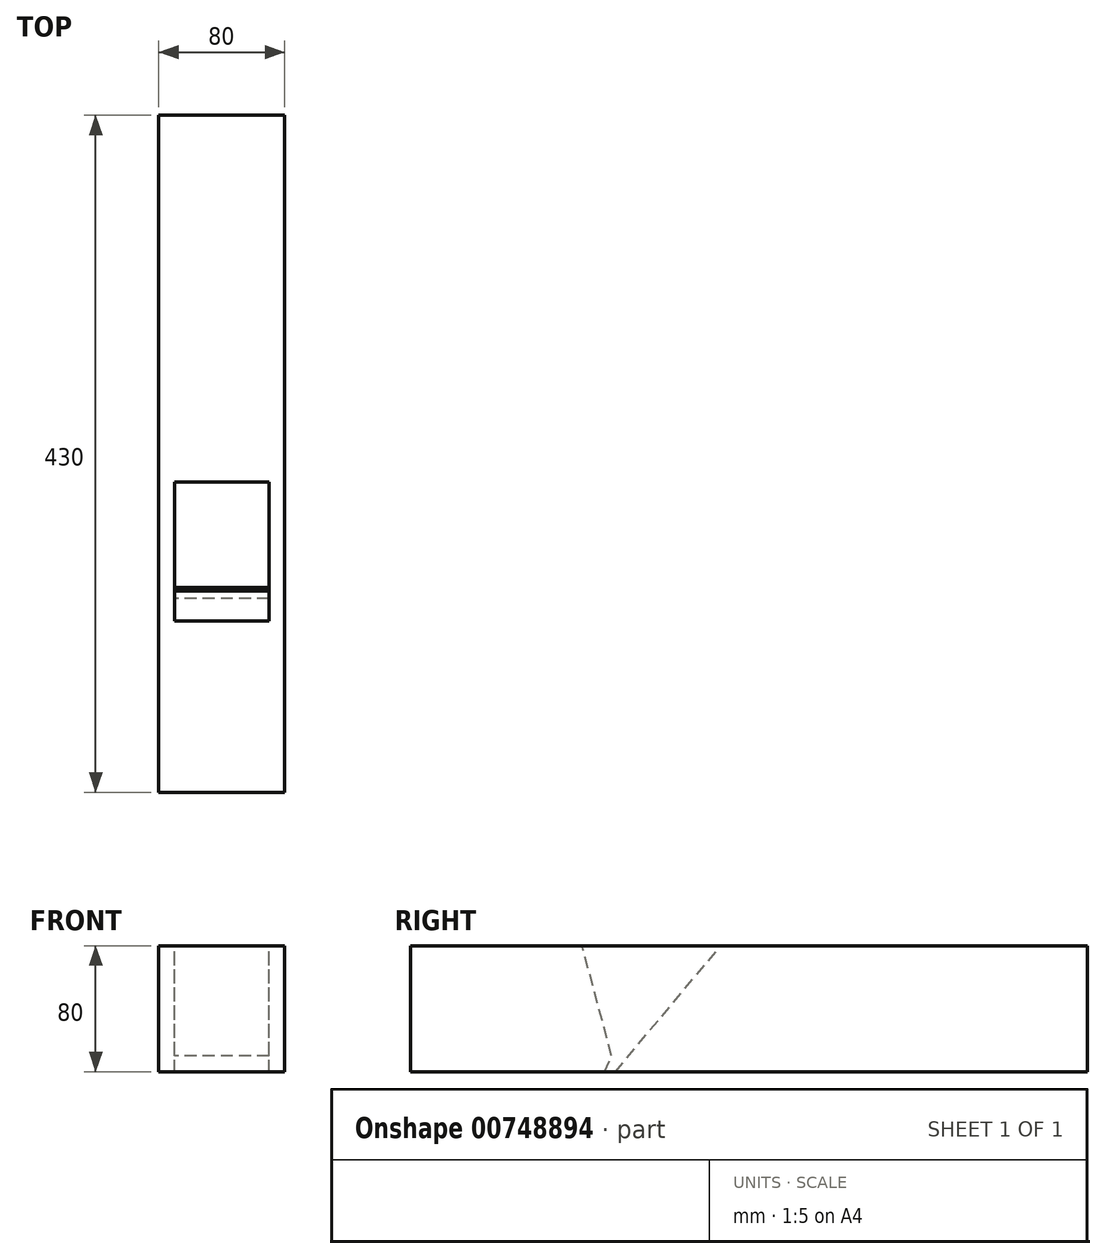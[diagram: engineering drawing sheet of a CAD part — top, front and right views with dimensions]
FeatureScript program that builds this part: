
annotation { "Feature Type Name" : "Feature", "Feature Type Description" : "" }
export const myFeature = defineFeature(function(context is Context, id is Id, definition is map)
    precondition{}
    {
        {
            var Q0;
            Q0=qCreatedBy(makeId("Right.planeOp"),FACE);
            var sketch = newSketch(context, id + "F0", { "sketchPlane" : qUnion([Q0])});
            skLineSegment(sketch, "E0.bottom", {"start": v(215, -40) * mm, "end": v(-215, -40) * mm});
            skLineSegment(sketch, "E0.top", {"start": v(215, 40) * mm, "end": v(-215, 40) * mm});
            skLineSegment(sketch, "E0.left", {"start": v(215, -40) * mm, "end": v(215, 40) * mm});
            skLineSegment(sketch, "E0.right", {"start": v(-215, -40) * mm, "end": v(-215, 40) * mm});
            skPoint(sketch, "E0.middle", {"position": v(0, 0) * mm});
            skSolve(sketch);
        }
        {
            var Q0;
            Q0=makeQuery(id+"F0.imprint","IMPRINT",FACE,{"disambiguationData":[TD([[makeQuery(id+"F0.imprint","IMPRINT",EDGE,{"derivedFrom":sQuery(id+"F0.wireOp",EDGE,"E0.bottom")}),-1.0]])]});
            extrude(context, id + "F1", {"entities" : qUnion([Q0]), "endBound" : BoundingType.SYMMETRIC, "depth" : 80 * mm, "offsetDistance" : 25 * mm});
        }
        {
            var Q0;
            Q0=qCreatedBy(makeId("Right.planeOp"),FACE);
            var sketch = newSketch(context, id + "F2", { "sketchPlane" : qUnion([Q0])});
            skLineSegment(sketch, "E1.bottom", {"start": v(-85, -40) * mm, "end": v(-92, -40) * mm});
            skLineSegment(sketch, "E1.left", {"start": v(215, -40) * mm, "end": v(215, 40) * mm});
            skPoint(sketch, "E1.middle", {"position": v(0, 0) * mm});
            skLineSegment(sketch, "E2", {"start": v(-92, -40) * mm, "end": v(-85, -40) * mm});
            skLineSegment(sketch, "E3", {"start": v(-85, -40) * mm, "end": v(-17.87, 40) * mm});
            skLineSegment(sketch, "E4", {"start": v(-92, -40) * mm, "end": v(-87.34, -30) * mm});
            skLineSegment(sketch, "E5", {"start": v(-87.34, -30) * mm, "end": v(-106.1, 40) * mm});
            skLineSegment(sketch, "E6", {"start": v(-106.1, 40) * mm, "end": v(-106.1, 50) * mm});
            skLineSegment(sketch, "E7", {"start": v(-106.1, 50) * mm, "end": v(-17.87, 50) * mm});
            skLineSegment(sketch, "E8", {"start": v(-17.87, 50) * mm, "end": v(-17.87, 40) * mm});
            skLineSegment(sketch, "E9", {"start": v(-92, -40) * mm, "end": v(-92, -57.64) * mm});
            skLineSegment(sketch, "E10", {"start": v(-92, -57.64) * mm, "end": v(-85, -57.64) * mm});
            skLineSegment(sketch, "E11", {"start": v(-85, -57.64) * mm, "end": v(-85, -40) * mm});
            skSolve(sketch);
        }
        {
            var Q0;
            Q0 = qSketchRegion(id + "F2", true);
            extrude(context, id + "F3", {"entities" : qUnion([Q0]), "operationType" : NewBodyOperationType.REMOVE, "endBound" : BoundingType.SYMMETRIC, "depth" : 60 * mm, "offsetDistance" : 25 * mm});
        }
    });
